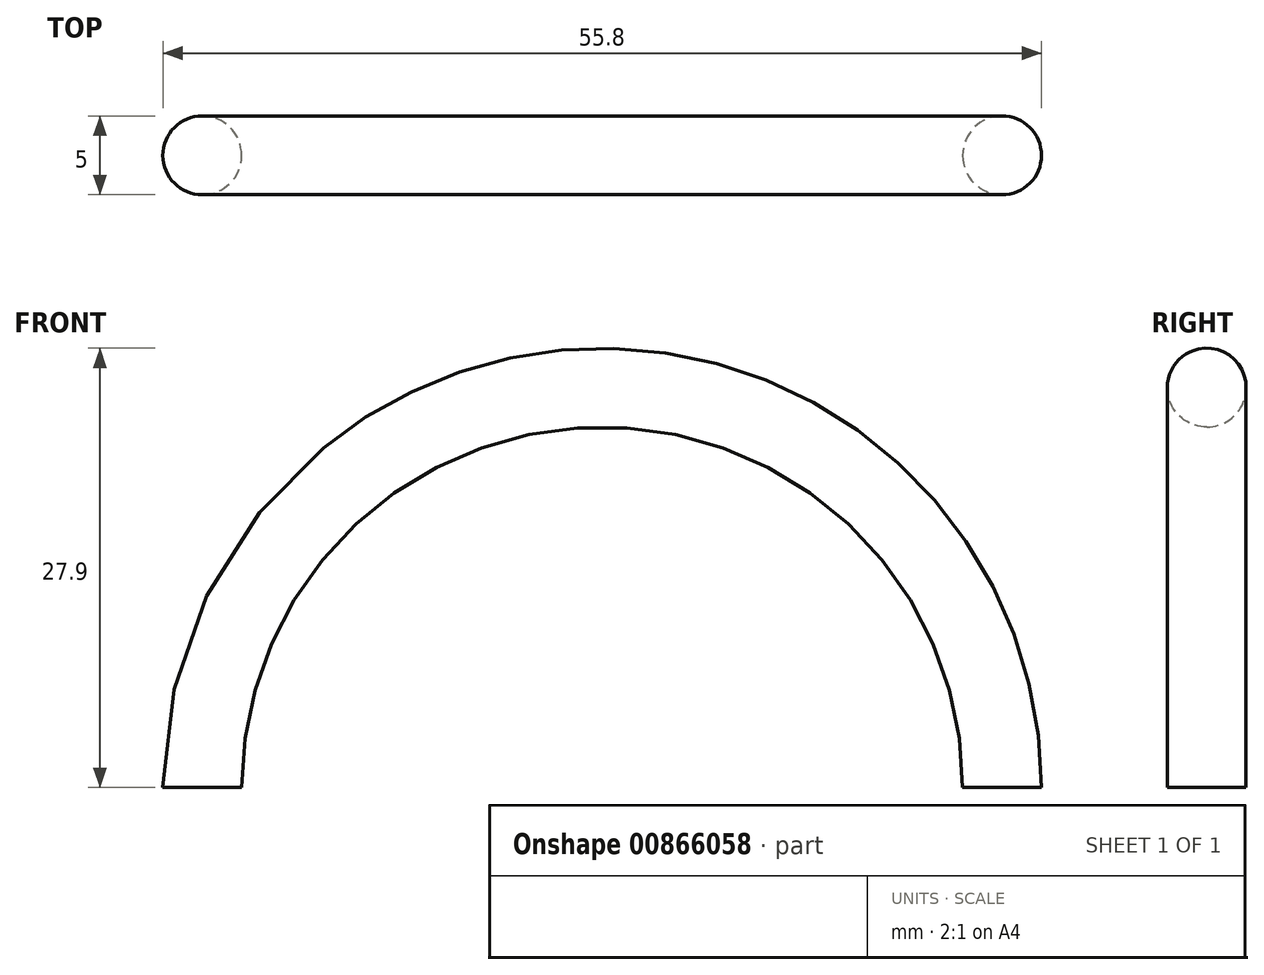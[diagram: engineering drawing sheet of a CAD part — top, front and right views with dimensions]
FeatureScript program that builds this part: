
annotation { "Feature Type Name" : "Feature", "Feature Type Description" : "" }
export const myFeature = defineFeature(function(context is Context, id is Id, definition is map)
    precondition{}
    {
        {
            var Q0;
            Q0=qCreatedBy(makeId("Front.planeOp"),FACE);
            var sketch = newSketch(context, id + "F0", { "sketchPlane" : qUnion([Q0])});
            skArc(sketch, "E0", {"start": v(50.8, 0) * mm, "mid": v(25.4, 25.4) * mm, "end": v(0, 0) * mm});
            skSolve(sketch);
        }
        {
            var Q0;
            Q0=qCreatedBy(makeId("Top.planeOp"),FACE);
            var sketch = newSketch(context, id + "F1", { "sketchPlane" : qUnion([Q0])});
            skCircle(sketch, "E1", {"center": v(0, 0) * mm, "radius": 2.5 * mm});
            skSolve(sketch);
        }
        {
            var Q0;
            Q0=makeQuery(id+"F1.imprint","IMPRINT",FACE,{"disambiguationData":[TD([[makeQuery(id+"F1.imprint","IMPRINT",EDGE,{"derivedFrom":sQuery(id+"F1.wireOp",EDGE,"E1")}),1.0]])]});
            var Q1;
            Q1=qConstructionFilter(qBodyType(qCreatedBy(id+"F0",EDGE),BodyType.WIRE),ConstructionObject.NO);
            sweep(context, id + "F2", {"profiles" : qUnion([Q0]), "path" : qUnion([Q1])});
        }
    });
